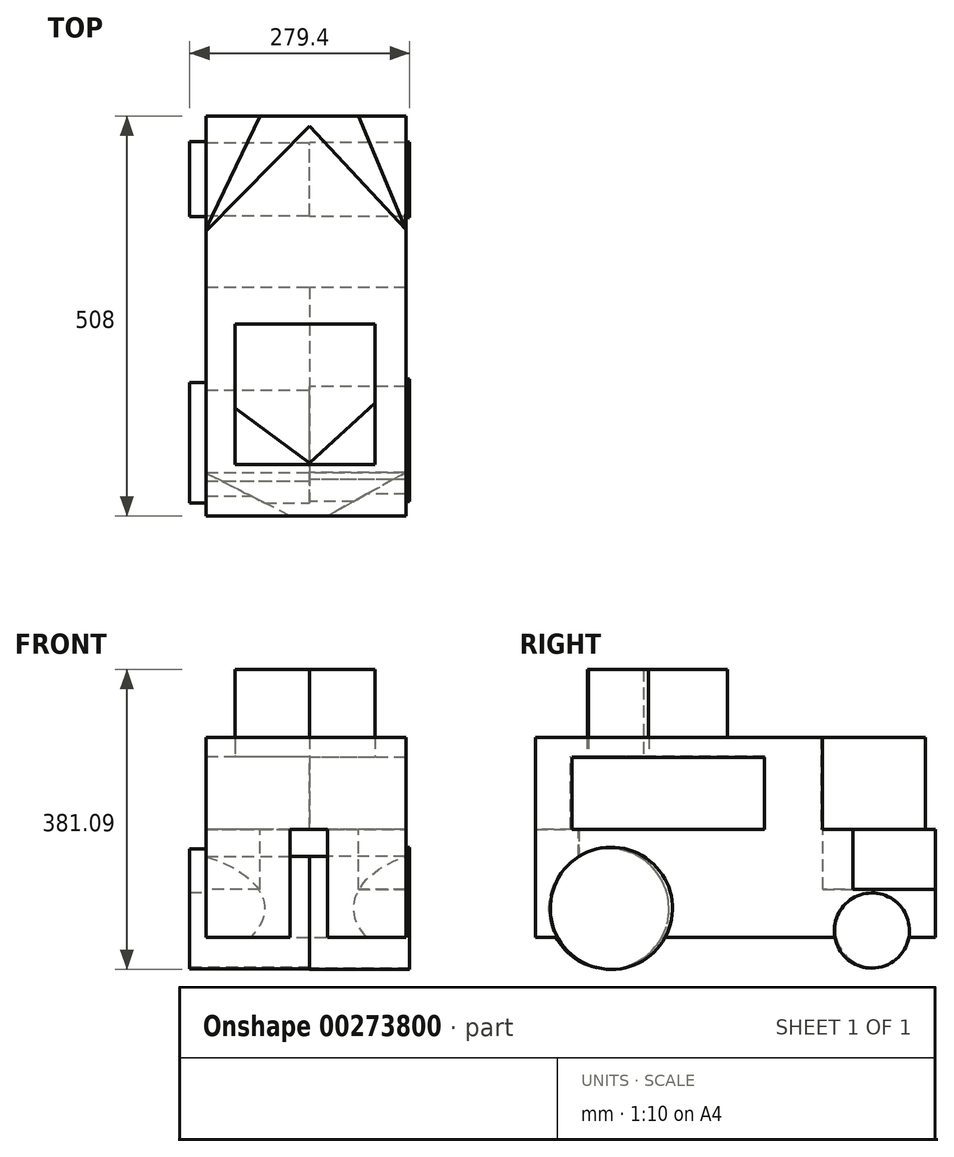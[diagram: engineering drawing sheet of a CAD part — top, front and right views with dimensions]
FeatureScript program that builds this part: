
annotation { "Feature Type Name" : "Feature", "Feature Type Description" : "" }
export const myFeature = defineFeature(function(context is Context, id is Id, definition is map)
    precondition{}
    {
        {
            var Q0;
            Q0=qCreatedBy(makeId("Front.planeOp"),FACE);
            var sketch = newSketch(context, id + "F0", { "sketchPlane" : qUnion([Q0])});
            skLineSegment(sketch, "E0.bottom", {"start": v(-131.82, 117.08) * mm, "end": v(122.18, 117.08) * mm});
            skLineSegment(sketch, "E0.top", {"start": v(-131.82, -136.92) * mm, "end": v(122.18, -136.92) * mm});
            skLineSegment(sketch, "E0.left", {"start": v(-131.82, 117.08) * mm, "end": v(-131.82, -136.92) * mm});
            skLineSegment(sketch, "E0.right", {"start": v(122.18, 117.08) * mm, "end": v(122.18, -136.92) * mm});
            skSolve(sketch);
        }
        {
            var Q0;
            Q0 = qSketchRegion(id + "F0", true);
            extrude(context, id + "F1", {"entities" : qUnion([Q0]), "depth" : 508 * mm});
        }
        {
            var Q0;
            Q0=qCreatedBy(makeId("Top.planeOp"),FACE);
            var sketch = newSketch(context, id + "F2", { "sketchPlane" : qUnion([Q0])});
            skLineSegment(sketch, "E1.bottom", {"start": v(-95.1, -264.25) * mm, "end": v(82.7, -264.25) * mm});
            skLineSegment(sketch, "E1.top", {"start": v(-95.1, -442.05) * mm, "end": v(82.7, -442.05) * mm});
            skLineSegment(sketch, "E1.left", {"start": v(-95.1, -264.25) * mm, "end": v(-95.1, -442.05) * mm});
            skLineSegment(sketch, "E1.right", {"start": v(82.7, -264.25) * mm, "end": v(82.7, -442.05) * mm});
            skSolve(sketch);
        }
        {
            var Q0;
            Q0 = qSketchRegion(id + "F2", true);
            extrude(context, id + "F3", {"entities" : qUnion([Q0]), "operationType" : NewBodyOperationType.ADD, "depth" : 203.2 * mm});
        }
        {
            var Q0;
            Q0=qCreatedBy(makeId("Top.planeOp"),FACE);
            var sketch = newSketch(context, id + "F4", { "sketchPlane" : qUnion([Q0])});
            skLineSegment(sketch, "E2", {"start": v(0, -12.96) * mm, "end": v(-132.92, -147.03) * mm});
            skLineSegment(sketch, "E3", {"start": v(-132.92, -147.03) * mm, "end": v(-132.92, 0) * mm});
            skLineSegment(sketch, "E4", {"start": v(-132.92, 0) * mm, "end": v(123.28, 0) * mm});
            skLineSegment(sketch, "E5", {"start": v(0, -12.96) * mm, "end": v(0, 0) * mm});
            skLineSegment(sketch, "E6", {"start": v(0, -12.96) * mm, "end": v(123.29, -145.2) * mm});
            skLineSegment(sketch, "E7", {"start": v(123.29, -145.2) * mm, "end": v(123.28, 0) * mm});
            skSolve(sketch);
        }
        {
            var Q0;
            Q0 = qSketchRegion(id + "F4", true);
            extrude(context, id + "F5", {"entities" : qUnion([Q0]), "operationType" : NewBodyOperationType.REMOVE, "depth" : 127 * mm});
        }
        {
            var Q0;
            Q0=qCreatedBy(makeId("Top.planeOp"),FACE);
            var sketch = newSketch(context, id + "F6", { "sketchPlane" : qUnion([Q0])});
            skLineSegment(sketch, "E8", {"start": v(-63.13, 0) * mm, "end": v(-132.92, -145.2) * mm});
            skLineSegment(sketch, "E9", {"start": v(121.44, -143.36) * mm, "end": v(61.75, 0) * mm});
            skLineSegment(sketch, "E10", {"start": v(-63.13, 0) * mm, "end": v(-133.84, 0) * mm});
            skLineSegment(sketch, "E11", {"start": v(-133.84, 0) * mm, "end": v(-132.92, -145.2) * mm});
            skLineSegment(sketch, "E12", {"start": v(61.75, 0) * mm, "end": v(124.2, 0) * mm});
            skLineSegment(sketch, "E13", {"start": v(124.2, 0) * mm, "end": v(121.44, -143.36) * mm});
            skSolve(sketch);
        }
        {
            var Q0;
            Q0 = qSketchRegion(id + "F6", true);
            extrude(context, id + "F7", {"entities" : qUnion([Q0]), "operationType" : NewBodyOperationType.REMOVE, "oppositeDirection" : true, "depth" : 76.2 * mm});
        }
        {
            var Q0;
            Q0=qCreatedBy(makeId("Top.planeOp"),FACE);
            var sketch = newSketch(context, id + "F8", { "sketchPlane" : qUnion([Q0])});
            skLineSegment(sketch, "E14", {"start": v(-132.92, -452.82) * mm, "end": v(121.44, -452.82) * mm});
            skLineSegment(sketch, "E15", {"start": v(121.44, -452.82) * mm, "end": v(0, -520.77) * mm});
            skLineSegment(sketch, "E16", {"start": v(0, -520.77) * mm, "end": v(-132.92, -452.82) * mm});
            skSolve(sketch);
        }
        {
            var Q0;
            Q0 = qSketchRegion(id + "F8", true);
            extrude(context, id + "F9", {"entities" : qUnion([Q0]), "operationType" : NewBodyOperationType.REMOVE, "oppositeDirection" : true, "depth" : 254 * mm});
        }
        {
            var Q0;
            Q0=qCreatedBy(makeId("Right.planeOp"),FACE);
            var sketch = newSketch(context, id + "F10", { "sketchPlane" : qUnion([Q0])});
            skCircle(sketch, "E17", {"center": v(-411.88, -100.23) * mm, "radius": 77.65 * mm});
            skCircle(sketch, "E18", {"center": v(-80.96, -128.58) * mm, "radius": 47.73 * mm});
            skSolve(sketch);
        }
        {
            var Q0;
            Q0 = qSketchRegion(id + "F10", true);
            extrude(context, id + "F11", {"entities" : qUnion([Q0]), "operationType" : NewBodyOperationType.ADD, "depth" : 127 * mm});
        }
        {
            var Q0;
            Q0=qCreatedBy(makeId("Right.planeOp"),FACE);
            var sketch = newSketch(context, id + "F12", { "sketchPlane" : qUnion([Q0])});
            skCircle(sketch, "E19", {"center": v(-415.14, -100.81) * mm, "radius": 76.38 * mm});
            skCircle(sketch, "E20", {"center": v(-80.07, -127.51) * mm, "radius": 47.35 * mm});
            skSolve(sketch);
        }
        {
            var Q0;
            Q0 = qSketchRegion(id + "F12", true);
            extrude(context, id + "F13", {"entities" : qUnion([Q0]), "operationType" : NewBodyOperationType.ADD, "oppositeDirection" : true, "depth" : 152.4 * mm});
        }
        {
            var Q0;
            Q0=qCreatedBy(makeId("Top.planeOp"),FACE);
            var sketch = newSketch(context, id + "F14", { "sketchPlane" : qUnion([Q0])});
            skLineSegment(sketch, "E21", {"start": v(-94.89, -371.09) * mm, "end": v(0, -440.88) * mm});
            skLineSegment(sketch, "E22", {"start": v(-94.89, -371.09) * mm, "end": v(-94.89, -442.66) * mm});
            skLineSegment(sketch, "E23", {"start": v(-94.89, -442.66) * mm, "end": v(82.95, -442.66) * mm});
            skLineSegment(sketch, "E24", {"start": v(82.95, -442.66) * mm, "end": v(82.95, -364.32) * mm});
            skLineSegment(sketch, "E25", {"start": v(82.95, -364.32) * mm, "end": v(0, -440.88) * mm});
            skSolve(sketch);
        }
        {
            var Q0;
            Q0 = qSketchRegion(id + "F14", true);
            extrude(context, id + "F15", {"entities" : qUnion([Q0]), "operationType" : NewBodyOperationType.REMOVE, "depth" : 203.2 * mm});
        }
        {
            var Q0;
            Q0=qCreatedBy(makeId("Right.planeOp"),FACE);
            var sketch = newSketch(context, id + "F16", { "sketchPlane" : qUnion([Q0])});
            skLineSegment(sketch, "E26.bottom", {"start": v(-216.9, 0) * mm, "end": v(-463.87, 0) * mm});
            skLineSegment(sketch, "E26.top", {"start": v(-216.9, 92.75) * mm, "end": v(-463.87, 92.75) * mm});
            skLineSegment(sketch, "E26.left", {"start": v(-216.9, 0) * mm, "end": v(-216.9, 92.75) * mm});
            skLineSegment(sketch, "E26.right", {"start": v(-463.87, 0) * mm, "end": v(-463.87, 92.75) * mm});
            skSolve(sketch);
        }
        {
            var Q0;
            Q0 = qSketchRegion(id + "F16", true);
            extrude(context, id + "F17", {"entities" : qUnion([Q0]), "operationType" : NewBodyOperationType.REMOVE, "oppositeDirection" : true, "depth" : 152.4 * mm});
        }
        {
            var Q0;
            Q0=qCreatedBy(makeId("Right.planeOp"),FACE);
            var sketch = newSketch(context, id + "F18", { "sketchPlane" : qUnion([Q0])});
            skLineSegment(sketch, "E27.bottom", {"start": v(-217.57, 91.42) * mm, "end": v(-461.86, 91.42) * mm});
            skLineSegment(sketch, "E27.top", {"start": v(-217.57, 0) * mm, "end": v(-461.86, 0) * mm});
            skLineSegment(sketch, "E27.left", {"start": v(-217.57, 91.42) * mm, "end": v(-217.57, 0) * mm});
            skLineSegment(sketch, "E27.right", {"start": v(-461.86, 91.42) * mm, "end": v(-461.86, 0) * mm});
            skSolve(sketch);
        }
        {
            var Q0;
            Q0 = qSketchRegion(id + "F18", true);
            extrude(context, id + "F19", {"entities" : qUnion([Q0]), "operationType" : NewBodyOperationType.REMOVE, "depth" : 152.4 * mm});
        }
    });
